FCSTD DOCUMENT  (FreeCAD 0.22R37841 (Git))
Label: tacho
License: All rights reserved
LicenseURL: http://en.wikipedia.org/wiki/All_rights_reserved
objects: App::DocumentObjectGroup×3, App::Link×2, PartDesign::CoordinateSystem×1, App::FeaturePython×1, App::Part×1
note: 1 computed .brp shape members not serialized (recipe doc carries the construction recipe); baked Part::Feature solids carry a one-line shape summary decoded from their .brp
EXTERNAL_REF file=magcartrige.FCStd obj=LCS_Origin
EXTERNAL_REF file=magcartrige.FCStd obj=Part
EXTERNAL_REF file=cover.FCStd obj=LCS_Origin
EXTERNAL_REF file=cover.FCStd obj=Part

FEATURE [App::DocumentObjectGroup] Parts
FEATURE [PartDesign::CoordinateSystem] LCS_Origin
  AttacherType = Attacher::AttachEngine3D
  AttachmentSupport = -> [X_Axis]
  MapMode = 2
FEATURE [App::DocumentObjectGroup] Constraints
FEATURE [App::FeaturePython] Variables  # WARN: FeaturePython — macro-defined, semantics opaque (R4)
  Type = App::PropertyContainer
FEATURE [App::DocumentObjectGroup] Configurations
FEATURE [App::Link] cartrige
  AttachedBy = #LCS_Origin
  AttachedTo = Parent Assembly#LCS_Origin
  LinkedObject = -> <external magcartrige.FCStd>#Part
  SolverId = Asm4EE
  expr: Placement = LCS_Origin.Placement * AttachmentOffset * magcartrige#LCS_Origin.Placement ^ -1
FEATURE [App::Link] cover
  AttachedBy = #LCS_Origin
  AttachedTo = Parent Assembly#LCS_Origin
  LinkedObject = -> <external cover.FCStd>#Part
  SolverId = Asm4EE
  expr: Placement = LCS_Origin.Placement * AttachmentOffset * cover#LCS_Origin.Placement ^ -1
FEATURE [App::Part] Assembly
  AssemblyType = Part::Link
  Group = -> [LCS_Origin,Constraints,Variables,Configurations,cartrige,cover]
  Origin = -> Origin
  Type = Assembly

RESOLVED EXTERNAL PARTS (link-assembly join: the EXTERNAL_REF files above that resolve inside this repo's crawl, each included once):
---- part cover.FCStd = doc fcstd_a2f5109f2947 ----
FCSTD DOCUMENT  (FreeCAD 0.22R37841 (Git))
Label: cover
License: All rights reserved
LicenseURL: http://en.wikipedia.org/wiki/All_rights_reserved
objects: Sketcher::SketchObject×4, PartDesign::CoordinateSystem×2, PartDesign::Pocket×2, PartDesign::Revolution×1, PartDesign::Pad×1, PartDesign::PolarPattern×1, PartDesign::Body×1, App::Part×1
note: 16 computed .brp shape members not serialized (recipe doc carries the construction recipe); baked Part::Feature solids carry a one-line shape summary decoded from their .brp

FEATURE [PartDesign::CoordinateSystem] LCS_Origin
  AttacherType = Attacher::AttachEngine3D
  AttachmentSupport = -> [X_Axis]
  MapMode = 2
FEATURE [PartDesign::CoordinateSystem] LCS_Origin001
  AttacherType = Attacher::AttachEngine3D
  AttachmentSupport = -> [X_Axis001]
  MapMode = 2
FEATURE [Sketcher::SketchObject] Sketch
  AttachmentSupport = -> [XZ_Plane001]
  FullyConstrained = true
  MapMode = 5
  Placement = pos=(0,0,0) rot=(1,0,0;1.5708rad)
  sketch-geometry (8):
    g0: LineSegment StartX=0 StartY=0 StartZ=0 EndX=0 EndY=13 EndZ=0
    g1: LineSegment StartX=21.5 StartY=5 StartZ=0 EndX=21.5 EndY=3 EndZ=0
    g2: LineSegment StartX=21.5 StartY=3 StartZ=0 EndX=24 EndY=3 EndZ=0
    g3: LineSegment StartX=24 StartY=3 StartZ=0 EndX=24 EndY=13 EndZ=0
    g4: LineSegment StartX=23 StartY=13 StartZ=0 EndX=23 EndY=5 EndZ=0
    g5: LineSegment StartX=23 StartY=5 StartZ=0 EndX=21.5 EndY=5 EndZ=0
    g6: LineSegment StartX=24 StartY=13 StartZ=0 EndX=23 EndY=13 EndZ=0
    g7: GeomPoint X=21.5 Y=4 Z=0
  constraints (22):
    c: Coincident(g0,g-1)
    c: PointOnObject(g0,g-2)
    c: Coincident(g2,g1)
    c: Horizontal(g2)
    c: Coincident(g3,g2)
    c: Vertical(g3)
    c: Vertical(g4)
    c: Coincident(g5,g4)
    c: Coincident(g5,g1)
    c: Vertical(g1)
    c: DistanceX(g0,g4) = 23
    c: Horizontal(g5)
    c: Coincident(g6,g3)
    c: Horizontal(g6)
    c: DistanceY(g1,g1) = 2
    c: DistanceX(g0,g1) = 21.5
    c: Coincident(g6,g4)
    c: DistanceX(g0,g2) = 24
    c: DistanceY(g3,g3) = 10
    c: Symmetric(g1,g1,g7)
    c: DistanceY(g0,g7) = 4
    c: Horizontal(g4,g0)
FEATURE [PartDesign::Revolution] Revolution
  Angle = 360
  Angle2 = 60
  Axis = (0,2e-16,1)
  Base = (0,0,0)
  Placement = pos=(0,0,0) rot=(1,0,0;1.5708rad)
  Profile = -> Sketch
  ReferenceAxis = -> Sketch [V_Axis]
  Reversed = true
  Suppressed = false
  Type = 0
FEATURE [Sketcher::SketchObject] Sketch001
  AttachmentSupport = -> [XY_Plane001]
  FullyConstrained = true
  MapMode = 5
  sketch-geometry (9):
    g0: Circle CenterX=0 CenterY=0 CenterZ=0 NormalX=0 NormalY=0 NormalZ=1 AngleXU=0 Radius=17.5
    g1: Circle CenterX=-17.5 CenterY=0 CenterZ=0 NormalX=0 NormalY=0 NormalZ=1 AngleXU=0 Radius=2.625
    g2: Circle CenterX=-8.75 CenterY=15.1554 CenterZ=0 NormalX=0 NormalY=0 NormalZ=1 AngleXU=0 Radius=2.625
    g3: Circle CenterX=8.75 CenterY=15.1554 CenterZ=0 NormalX=0 NormalY=0 NormalZ=1 AngleXU=0 Radius=2.625
    g4: Circle CenterX=17.5 CenterY=0 CenterZ=0 NormalX=0 NormalY=0 NormalZ=1 AngleXU=0 Radius=2.625
    g5: Circle CenterX=8.75 CenterY=-15.1554 CenterZ=0 NormalX=0 NormalY=0 NormalZ=1 AngleXU=0 Radius=2.625
    g6: Circle CenterX=-8.75 CenterY=-15.1554 CenterZ=0 NormalX=0 NormalY=0 NormalZ=1 AngleXU=0 Radius=2.625
    g7: LineSegment StartX=-8.75 StartY=15.1554 StartZ=0 EndX=0 EndY=0 EndZ=0
    g8: LineSegment StartX=0 StartY=0 StartZ=0 EndX=8.75 EndY=-15.1554 EndZ=0
  constraints (24):
    c: Coincident(g0,g-1)
    c: PointOnObject(g1,g0)
    c: PointOnObject(g2,g0)
    c: PointOnObject(g3,g0)
    c: PointOnObject(g4,g0)
    c: PointOnObject(g5,g0)
    c: PointOnObject(g6,g0)
    c: PointOnObject(g1,g-1)
    c: PointOnObject(g4,g-1)
    c: Equal(g1,g2)
    c: Equal(g2,g3)
    c: Equal(g3,g4)
    c: Equal(g4,g5)
    c: Equal(g5,g6)
    c: Diameter(g4) = 5.25
    c: Coincident(g7,g2)
    c: Coincident(g7,g0)
    c: Coincident(g8,g0)
    c: Coincident(g8,g5)
    c: Parallel(g7,g8)
    c: Vertical(g2,g6)
    c: Vertical(g5,g3)
    c: Angle(g-1,g7) = 2.0944
    c: Diameter(g0) = 35
FEATURE [PartDesign::Pocket] Pocket
  BaseFeature = -> Revolution
  Direction = (0,0,-1)
  Length = 5.5
  Length2 = 5
  Placement = pos=(0,0,0) rot=(1,0,0;1.5708rad)
  Profile = -> Sketch001
  ReferenceAxis = -> Sketch001 [N_Axis]
  Reversed = true
  Suppressed = false
  Type = 0
FEATURE [Sketcher::SketchObject] Sketch002
  AttachmentSupport = -> [XY_Plane001]
  FullyConstrained = true
  MapMode = 5
  sketch-geometry (14):
    g0: LineSegment StartX=16.0346 StartY=12.7727 StartZ=0 EndX=-3.04425 EndY=20.2727 EndZ=0
    g1: LineSegment StartX=-3.04425 StartY=20.2727 StartZ=0 EndX=-19.0788 EndY=7.49996 EndZ=0
    g2: LineSegment StartX=-19.0788 StartY=7.49996 StartZ=0 EndX=-16.0346 EndY=-12.7727 EndZ=0
    g3: LineSegment StartX=-16.0346 StartY=-12.7727 StartZ=0 EndX=3.04425 EndY=-20.2727 EndZ=0
    g4: LineSegment StartX=3.04425 StartY=-20.2727 StartZ=0 EndX=19.0788 EndY=-7.49996 EndZ=0
    g5: LineSegment StartX=19.0788 StartY=-7.49996 StartZ=0 EndX=16.0346 EndY=12.7727 EndZ=0
    g6: Circle CenterX=0 CenterY=0 CenterZ=0 NormalX=0 NormalY=0 NormalZ=1 AngleXU=0 Radius=20.5
    g7: Circle CenterX=-3.04425 CenterY=20.2727 CenterZ=0 NormalX=0 NormalY=0 NormalZ=1 AngleXU=0 Radius=2.5
    g8: Circle CenterX=16.0346 CenterY=12.7727 CenterZ=0 NormalX=0 NormalY=0 NormalZ=1 AngleXU=0 Radius=2.5
    g9: Circle CenterX=19.0788 CenterY=-7.49996 CenterZ=0 NormalX=0 NormalY=0 NormalZ=1 AngleXU=0 Radius=2.5
    g10: Circle CenterX=3.04425 CenterY=-20.2727 CenterZ=0 NormalX=0 NormalY=0 NormalZ=1 AngleXU=0 Radius=2.5
    g11: Circle CenterX=-16.0346 CenterY=-12.7727 CenterZ=0 NormalX=0 NormalY=0 NormalZ=1 AngleXU=0 Radius=2.5
    g12: Circle CenterX=-19.0788 CenterY=7.49996 CenterZ=0 NormalX=0 NormalY=0 NormalZ=1 AngleXU=0 Radius=2.5
    g13: LineSegment StartX=0 StartY=0 StartZ=0 EndX=-19.0788 EndY=7.49996 EndZ=0
  constraints (30):
    c: Coincident(g0,g1)
    c: Coincident(g1,g2)
    c: Coincident(g2,g3)
    c: Coincident(g3,g4)
    c: Coincident(g4,g5)
    c: Coincident(g5,g0)
    c: Equal(g0, g1-g5) x5
    c: PointOnObject(g0,g6)
    c: PointOnObject(g1,g6)
    c: PointOnObject(g2,g6)
    c: PointOnObject(g3,g6)
    c: PointOnObject(g4,g6)
    c: PointOnObject(g5,g6)
    c: Coincident(g6,g-1)
    c: Coincident(g7,g0)
    c: Coincident(g8,g0)
    c: Coincident(g9,g4)
    c: Coincident(g10,g3)
    c: Coincident(g11,g2)
    c: Coincident(g12,g1)
    c: Equal(g12,g7)
    c: Equal(g7,g8)
    c: Equal(g8,g9)
    c: Equal(g9,g10)
    c: Equal(g10,g11)
    c: Diameter(g12) = 5
    c: Coincident(g13,g6)
    c: Coincident(g13,g12)
    c: Angle(g-1,g13) = 2.76704
    c: Distance(g13) = 20.5
FEATURE [Sketcher::SketchObject] Sketch003
  AttachmentOffset = pos=(0,0,3) rot=(0,0,1;0rad)
  AttachmentSupport = -> [XY_Plane001]
  FullyConstrained = true
  MapMode = 5
  Placement = pos=(0,0,3) rot=(0,0,1;0rad)
  sketch-geometry (7):
    g0: ArcOfCircle CenterX=0 CenterY=0 CenterZ=0 NormalX=0 NormalY=0 NormalZ=1 AngleXU=0 Radius=23 StartAngle=2.54967 EndAngle=2.98442
    g1: ArcOfCircle CenterX=-19.0788 CenterY=7.49996 CenterZ=0 NormalX=0 NormalY=0 NormalZ=1 AngleXU=0 Radius=3.89996 StartAngle=4.71239 EndAngle=7.10489
    g2: LineSegment StartX=-19.0788 StartY=3.6 StartZ=0 EndX=-22.7165 EndY=3.6 EndZ=0
    g3: LineSegment StartX=0 StartY=0 StartZ=0 EndX=-19.9186 EndY=11.5 EndZ=0
    g4: LineSegment StartX=0 StartY=0 StartZ=0 EndX=-19.0788 EndY=7.49996 EndZ=0
    g5: LineSegment StartX=-16.423 StartY=10.3559 StartZ=0 EndX=-19.0869 EndY=12.8331 EndZ=0
    g6: GeomPoint X=-9.15788 Y=3.6 Z=0
  constraints (18):
    c: Coincident(g0,g-1)
    c: Coincident(g2,g0)
    c: Tangent(g2,g1) = 1.5708
    c: Horizontal(g2)
    c: Coincident(g3,g0)
    c: PointOnObject(g3,g0)
    c: Angle(g-1,g3) = 2.61799
    c: Radius(g0) = 23
    c: DistanceY(g0,g0) = 3.6
    c: Coincident(g4,g0)
    c: Coincident(g4,g1)
    c: Angle(g-1,g4) = 2.76704
    c: Distance(g4) = 20.5
    c: Coincident(g5,g0)
    c: Tangent(g5,g1) = -1.5708
    c: PointOnObject(g6,g4)
    c: PointOnObject(g6,g2)
    c: PointOnObject(g6,g5)
FEATURE [PartDesign::Pad] Pad
  BaseFeature = -> Pocket
  Direction = (0,0,1)
  Length = 3
  Length2 = 10
  Placement = pos=(0,0,0) rot=(1,0,0;1.5708rad)
  Profile = -> Sketch003
  ReferenceAxis = -> Sketch003 [N_Axis]
  Suppressed = false
  Type = 0
FEATURE [PartDesign::PolarPattern] PolarPattern
  Angle = 360
  Axis = -> Sketch003 [N_Axis]
  BaseFeature = -> Pad
  Mode = 0
  Occurrences = 3
  Offset = 120
  Originals = -> [Pad]
  Placement = pos=(0,0,0) rot=(1,0,0;1.5708rad)
  Suppressed = false
  TransformMode = 0
FEATURE [PartDesign::Pocket] Pocket001
  BaseFeature = -> PolarPattern
  Direction = (0,0,-1)
  Length = 5
  Length2 = 5
  Placement = pos=(0,0,0) rot=(1,0,0;1.5708rad)
  Profile = -> Sketch002
  ReferenceAxis = -> Sketch002 [N_Axis]
  Reversed = true
  Suppressed = false
  Type = 1
FEATURE [PartDesign::Body] Body
  AllowCompound = false
  Group = -> [LCS_Origin001,Sketch,Revolution,Sketch001,Pocket,Sketch003,Pad,PolarPattern,Sketch002,Pocket001]
  Origin = -> Origin001
  Tip = -> Pocket001
FEATURE [App::Part] Part
  Group = -> [LCS_Origin,Body]
  Origin = -> Origin
---- part magcartrige.FCStd = doc fcstd_ac319c4ce95f ----
FCSTD DOCUMENT  (FreeCAD 0.22R37841 (Git))
Label: magcartrige
License: All rights reserved
LicenseURL: http://en.wikipedia.org/wiki/All_rights_reserved
objects: Sketcher::SketchObject×3, PartDesign::CoordinateSystem×2, PartDesign::Revolution×1, PartDesign::Pocket×1, PartDesign::Hole×1, PartDesign::Body×1, App::Part×1
note: 12 computed .brp shape members not serialized (recipe doc carries the construction recipe); baked Part::Feature solids carry a one-line shape summary decoded from their .brp

FEATURE [PartDesign::CoordinateSystem] LCS_Origin
  AttacherType = Attacher::AttachEngine3D
  AttachmentSupport = -> [X_Axis]
  MapMode = 2
FEATURE [PartDesign::CoordinateSystem] LCS_Origin001
  AttacherType = Attacher::AttachEngine3D
  AttachmentSupport = -> [X_Axis001]
  MapMode = 2
FEATURE [Sketcher::SketchObject] Sketch
  AttachmentSupport = -> [XZ_Plane001]
  FullyConstrained = true
  MapMode = 5
  Placement = pos=(0,0,0) rot=(1,0,0;1.5708rad)
  sketch-geometry (5):
    g0: LineSegment StartX=0 StartY=0 StartZ=0 EndX=0 EndY=1.7 EndZ=0
    g1: LineSegment StartX=8.9 StartY=0 StartZ=0 EndX=8.9 EndY=1.7 EndZ=0
    g2: LineSegment StartX=24 StartY=0 StartZ=0 EndX=8.9 EndY=0 EndZ=0
    g3: LineSegment StartX=24 StartY=1.7 StartZ=0 EndX=24 EndY=0 EndZ=0
    g4: LineSegment StartX=8.9 StartY=1.7 StartZ=0 EndX=24 EndY=1.7 EndZ=0
  constraints (15):
    c: Coincident(g0,g-1)
    c: PointOnObject(g0,g-2)
    c: PointOnObject(g1,g-1)
    c: PointOnObject(g2,g-1)
    c: Coincident(g2,g1)
    c: Vertical(g1)
    c: DistanceX(g0,g1) = 8.9
    c: DistanceX(g0,g2) = 24
    c: Coincident(g3,g2)
    c: Vertical(g3)
    c: Coincident(g4,g1)
    c: Horizontal(g4)
    c: DistanceY(g3,g3) = 1.7
    c: PointOnObject(g0,g4)
    c: Coincident(g4,g3)
FEATURE [PartDesign::Revolution] Revolution
  Angle = 360
  Angle2 = 60
  Axis = (0,2e-16,1)
  Base = (0,0,0)
  Placement = pos=(0,0,0) rot=(1,0,0;1.5708rad)
  Profile = -> Sketch
  ReferenceAxis = -> Sketch [V_Axis]
  Reversed = true
  Suppressed = false
  Type = 0
FEATURE [Sketcher::SketchObject] Sketch001
  AttachmentOffset = pos=(0,0,0.3) rot=(0,0,1;0rad)
  AttachmentSupport = -> [XY_Plane001]
  FullyConstrained = true
  MapMode = 5
  Placement = pos=(0,0,0.3) rot=(0,0,1;0rad)
  sketch-geometry (25):
    g0: LineSegment StartX=16.2872 StartY=-6.40122 StartZ=0 EndX=2.6 EndY=17.3058 EndZ=0
    g1: LineSegment StartX=2.6 StartY=17.3058 StartZ=0 EndX=-2.6 EndY=17.3058 EndZ=0
    g2: LineSegment StartX=-2.6 StartY=17.3058 StartZ=0 EndX=-16.2872 EndY=-6.40122 EndZ=0
    g3: LineSegment StartX=-16.2872 StartY=-6.40122 StartZ=0 EndX=-13.6872 EndY=-10.9046 EndZ=0
    g4: LineSegment StartX=-13.6872 StartY=-10.9046 StartZ=0 EndX=13.6872 EndY=-10.9046 EndZ=0
    g5: LineSegment StartX=13.6872 StartY=-10.9046 StartZ=0 EndX=16.2872 EndY=-6.40122 EndZ=0
    g6: Circle CenterX=0 CenterY=0 CenterZ=0 NormalX=0 NormalY=0 NormalZ=1 AngleXU=0 Radius=17.5
    g7: ArcOfCircle CenterX=-16.2872 CenterY=-6.40122 CenterZ=0 NormalX=0 NormalY=0 NormalZ=1 AngleXU=0 Radius=2.6 StartAngle=1.44895 EndAngle=4.4722
    g8: ArcOfCircle CenterX=-17.1436 CenterY=-9.89788 CenterZ=0 NormalX=0 NormalY=0 NormalZ=1 AngleXU=0 Radius=1 StartAngle=5.99977 EndAngle=7.61379
    g9: ArcOfCircle CenterX=-15.8497 CenterY=-2.82791 CenterZ=0 NormalX=0 NormalY=0 NormalZ=1 AngleXU=0 Radius=1 StartAngle=4.59055 EndAngle=6.45975
    g10: ArcOfCircle CenterX=0 CenterY=0 CenterZ=0 NormalX=0 NormalY=0 NormalZ=1 AngleXU=0 Radius=15.1 StartAngle=1.91783 EndAngle=3.31816
    g11: ArcOfCircle CenterX=-2.6 CenterY=17.3058 CenterZ=0 NormalX=0 NormalY=0 NormalZ=1 AngleXU=0 Radius=2.6 StartAngle=0.763786 EndAngle=3.78703
    g12: ArcOfCircle CenterX=-5.4758 CenterY=15.1402 CenterZ=0 NormalX=0 NormalY=0 NormalZ=1 AngleXU=0 Radius=1 StartAngle=5.05943 EndAngle=6.92863
    g13: ArcOfCircle CenterX=2.6 CenterY=17.3058 CenterZ=0 NormalX=0 NormalY=0 NormalZ=1 AngleXU=0 Radius=2.6 StartAngle=5.63774 EndAngle=8.66099
    g14: ArcOfCircle CenterX=0 CenterY=0 CenterZ=0 NormalX=0 NormalY=0 NormalZ=1 AngleXU=0 Radius=15.1 StartAngle=6.10662 EndAngle=7.50695
    g15: ArcOfCircle CenterX=16.2872 CenterY=-6.40122 CenterZ=0 NormalX=0 NormalY=0 NormalZ=1 AngleXU=0 Radius=2.6 StartAngle=4.95258 EndAngle=7.97582
    g16: ArcOfCircle CenterX=13.6872 CenterY=-10.9046 CenterZ=0 NormalX=0 NormalY=0 NormalZ=1 AngleXU=0 Radius=2.6 StartAngle=3.54335 EndAngle=6.5666
    g17: ArcOfCircle CenterX=0 CenterY=0 CenterZ=0 NormalX=0 NormalY=0 NormalZ=1 AngleXU=0 Radius=15.1 StartAngle=4.01223 EndAngle=5.41255
    g18: ArcOfCircle CenterX=-13.6872 CenterY=-10.9046 CenterZ=0 NormalX=0 NormalY=0 NormalZ=1 AngleXU=0 Radius=2.6 StartAngle=2.85818 EndAngle=5.88143
    g19: ArcOfCircle CenterX=-3.2e-15 CenterY=19.7958 CenterZ=0 NormalX=0 NormalY=0 NormalZ=1 AngleXU=0 Radius=1 StartAngle=3.90538 EndAngle=5.5194
    g20: ArcOfCircle CenterX=5.4758 CenterY=15.1402 CenterZ=0 NormalX=0 NormalY=0 NormalZ=1 AngleXU=0 Radius=1 StartAngle=2.49615 EndAngle=4.36535
    g21: ArcOfCircle CenterX=15.8497 CenterY=-2.82791 CenterZ=0 NormalX=0 NormalY=0 NormalZ=1 AngleXU=0 Radius=1 StartAngle=2.96503 EndAngle=4.83423
    g22: ArcOfCircle CenterX=17.1436 CenterY=-9.89788 CenterZ=0 NormalX=0 NormalY=0 NormalZ=1 AngleXU=0 Radius=1 StartAngle=1.81098 EndAngle=3.425
    g23: ArcOfCircle CenterX=10.3739 CenterY=-12.3123 CenterZ=0 NormalX=0 NormalY=0 NormalZ=1 AngleXU=0 Radius=1 StartAngle=0.401757 EndAngle=2.27096
    g24: ArcOfCircle CenterX=-10.3739 CenterY=-12.3123 CenterZ=0 NormalX=0 NormalY=0 NormalZ=1 AngleXU=0 Radius=1 StartAngle=0.870635 EndAngle=2.73984
  constraints (65):
    c: Coincident(g0,g1)
    c: Coincident(g1,g2)
    c: Coincident(g2,g3)
    c: Coincident(g3,g4)
    c: Coincident(g4,g5)
    c: Coincident(g5,g0)
    c: PointOnObject(g0,g6)
    c: PointOnObject(g1,g6)
    c: PointOnObject(g2,g6)
    c: PointOnObject(g3,g6)
    c: PointOnObject(g4,g6)
    c: Coincident(g6,g-1)
    c: Diameter(g6) = 35
    c: Coincident(g7,g2)
    c: Coincident(g10,g6)
    c: Coincident(g11,g1)
    c: Tangent(g11,g12) = 1.5708
    c: Tangent(g10,g12) = 1.5708
    c: Coincident(g13,g0)
    c: Coincident(g14,g6)
    c: Coincident(g15,g0)
    c: Coincident(g16,g4)
    c: Coincident(g17,g6)
    c: Coincident(g18,g3)
    c: Tangent(g8,g7) = 1.5708
    c: Tangent(g9,g10) = 1.5708
    c: Tangent(g9,g7) = 1.5708
    c: Tangent(g11,g19) = 1.5708
    c: Tangent(g13,g20) = 1.5708
    c: Tangent(g14,g20) = 1.5708
    c: Tangent(g14,g21) = 1.5708
    c: Tangent(g15,g21) = 1.5708
    c: Tangent(g15,g22) = 1.5708
    c: Tangent(g16,g23) = 1.5708
    c: Tangent(g17,g23) = 1.5708
    c: Tangent(g17,g24) = 1.5708
    c: Tangent(g18,g24) = 1.5708
    c: Equal(g8,g9)
    c: Equal(g23,g24)
    c: Radius(g7) = 2.6
    c: Radius(g8) = 1
    c: Equal(g7,g11)
    c: Equal(g11,g13)
    c: Equal(g13,g15)
    c: Equal(g15,g16)
    c: Equal(g16,g18)
    c: Horizontal(g1)
    c: Tangent(g19,g13) = 1.5708
    c: PointOnObject(g0,g6)
    c: Horizontal(g4)
    c: Tangent(g13,g11)
    c: Tangent(g8,g18) = 1.5708
    c: Tangent(g16,g22) = 1.5708
    c: Tangent(g7,g18)
    c: Tangent(g15,g16)
    c: Equal(g2,g4)
    c: Equal(g17,g10)
    c: Equal(g10,g14)
    c: Equal(g8,g24)
    c: Equal(g23,g22)
    c: Equal(g22,g21)
    c: Equal(g9,g12)
    c: Equal(g12,g20)
    c: Equal(g19,g12)
    c: Radius(g14) = 15.1
FEATURE [PartDesign::Pocket] Pocket
  BaseFeature = -> Revolution
  Direction = (0,0,-1)
  Length = 5.2
  Length2 = 5
  Placement = pos=(0,0,0) rot=(1,0,0;1.5708rad)
  Profile = -> Sketch001
  ReferenceAxis = -> Sketch001 [N_Axis]
  Reversed = true
  Suppressed = false
  Type = 0
FEATURE [Sketcher::SketchObject] Sketch002
  AttachmentSupport = -> [XY_Plane001]
  FullyConstrained = true
  MapMode = 5
  sketch-geometry (7):
    g0: Circle CenterX=0 CenterY=0 CenterZ=0 NormalX=0 NormalY=0 NormalZ=1 AngleXU=0 Radius=17.5
    g1: Circle CenterX=-8.75 CenterY=15.1554 CenterZ=0 NormalX=0 NormalY=0 NormalZ=1 AngleXU=0 Radius=1.35
    g2: Circle CenterX=-8.75 CenterY=-15.1554 CenterZ=0 NormalX=0 NormalY=0 NormalZ=1 AngleXU=0 Radius=1.35
    g3: Circle CenterX=17.5 CenterY=1.034e-13 CenterZ=0 NormalX=0 NormalY=0 NormalZ=1 AngleXU=0 Radius=1.35
    g4: LineSegment StartX=0 StartY=0 StartZ=0 EndX=17.5 EndY=1.034e-13 EndZ=0
    g5: LineSegment StartX=0 StartY=0 StartZ=0 EndX=-8.75 EndY=15.1554 EndZ=0
    g6: LineSegment StartX=-8.75 StartY=-15.1554 StartZ=0 EndX=0 EndY=0 EndZ=0
  constraints (17):
    c: Coincident(g0,g-1)
    c: PointOnObject(g2,g0)
    c: PointOnObject(g3,g0)
    c: Equal(g1,g2)
    c: Equal(g1,g3)
    c: Diameter(g0) = 35
    c: Diameter(g3) = 2.7
    c: Coincident(g4,g0)
    c: Coincident(g4,g3)
    c: Coincident(g5,g0)
    c: Coincident(g5,g1)
    c: Coincident(g6,g2)
    c: Coincident(g6,g0)
    c: PointOnObject(g1,g0)
    c: Angle(g6,g4) = 2.0944
    c: Angle(g4,g5) = 2.0944
    c: Angle(g-2,g5) = 0.523599
FEATURE [PartDesign::Hole] Hole
  BaseFeature = -> Pocket
  CustomThreadClearance = 0
  Depth = 136.998
  DepthType = 1
  Diameter = 2.7
  DrillForDepth = false
  DrillPoint = 1
  DrillPointAngle = 118
  HoleCutCountersinkAngle = 90
  HoleCutCustomValues = false
  HoleCutDepth = 0.7
  HoleCutDiameter = 4.7
  HoleCutType = 1
  ModelThread = false
  Placement = pos=(0,0,0) rot=(1,0,0;1.5708rad)
  Profile = -> Sketch002
  Reversed = true
  Suppressed = false
  Tapered = false
  TaperedAngle = 90
  ThreadClass = 0
  ThreadDepth = 136.998
  ThreadDepthType = 0
  ThreadDirection = 0
  ThreadFit = 1
  ThreadSize = 8
  ThreadType = 1
  Threaded = false
  UseCustomThreadClearance = false
FEATURE [PartDesign::Body] Body
  AllowCompound = false
  Group = -> [LCS_Origin001,Sketch,Revolution,Sketch001,Pocket,Sketch002,Hole]
  Origin = -> Origin001
  Tip = -> Hole
FEATURE [App::Part] Part
  Group = -> [LCS_Origin,Body]
  Origin = -> Origin
